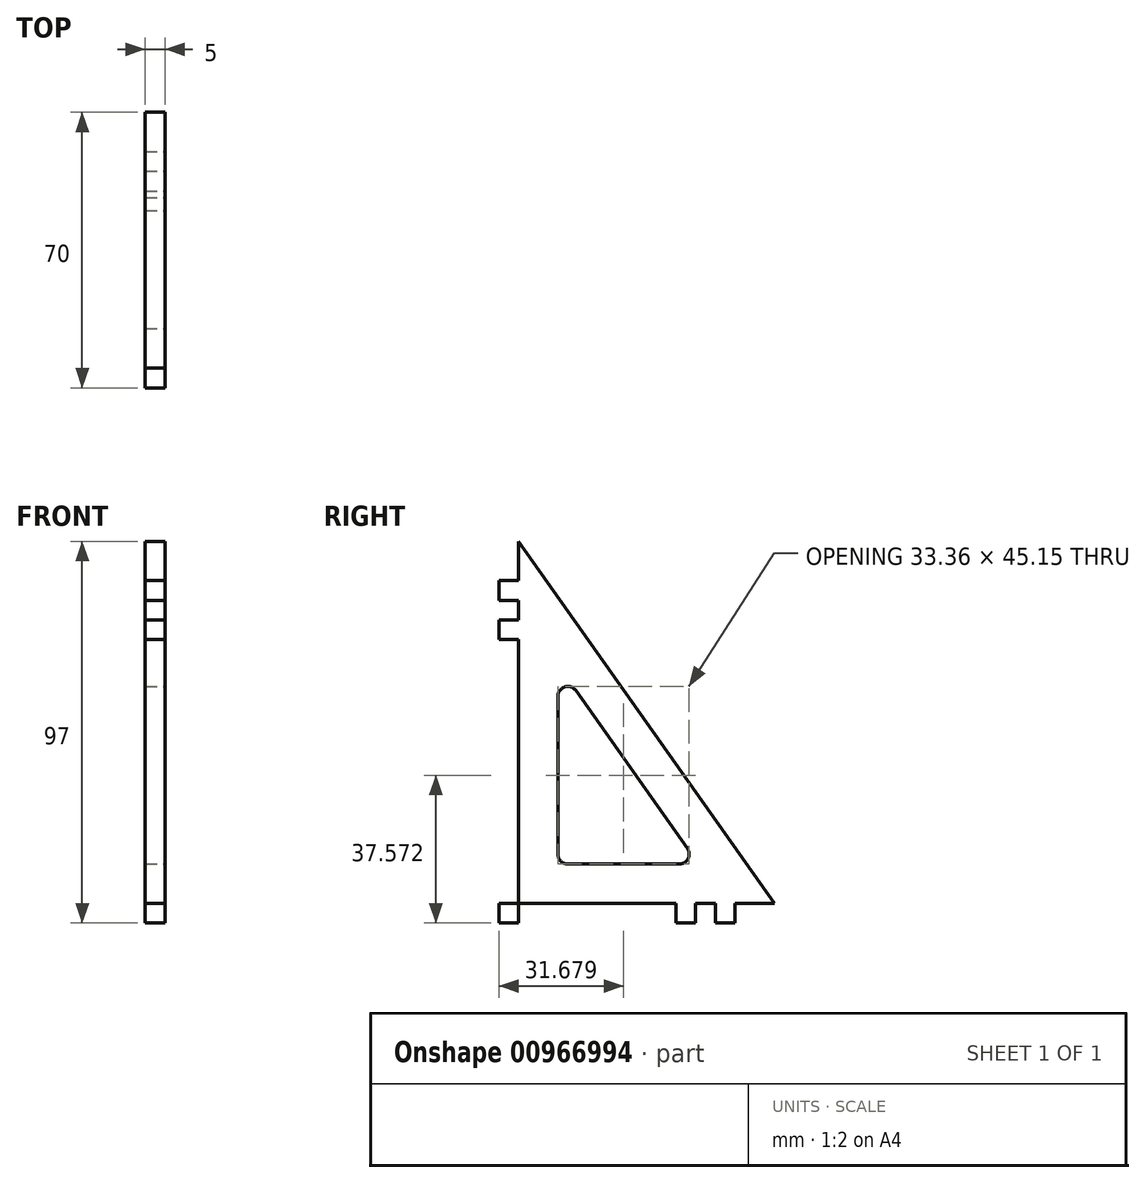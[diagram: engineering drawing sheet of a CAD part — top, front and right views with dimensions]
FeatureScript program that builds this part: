
annotation { "Feature Type Name" : "Feature", "Feature Type Description" : "" }
export const myFeature = defineFeature(function(context is Context, id is Id, definition is map)
    precondition{}
    {
        {
            var Q0;
            Q0=qCreatedBy(makeId("Right.planeOp"),FACE);
            var sketch = newSketch(context, id + "F0", { "sketchPlane" : qUnion([Q0])});
            skLineSegment(sketch, "E0", {"start": v(0, 97) * mm, "end": v(0, 0) * mm});
            skLineSegment(sketch, "E1", {"start": v(0, 0) * mm, "end": v(70, 0) * mm});
            skLineSegment(sketch, "E2", {"start": v(70, 0) * mm, "end": v(70, 5) * mm});
            skLineSegment(sketch, "E3", {"start": v(70, 5) * mm, "end": v(5, 97) * mm});
            skLineSegment(sketch, "E4", {"start": v(5, 97) * mm, "end": v(0, 97) * mm});
            skSolve(sketch);
        }
        {
            var Q0;
            Q0=makeQuery(id+"F0.imprint","IMPRINT",FACE,{"disambiguationData":[TD([[makeQuery(id+"F0.imprint","IMPRINT",EDGE,{"derivedFrom":sQuery(id+"F0.wireOp",EDGE,"E0")}),1.0]])]});
            extrude(context, id + "F1", {"entities" : qUnion([Q0]), "oppositeDirection" : true, "depth" : 5 * mm, "offsetDistance" : 25 * mm});
        }
        {
            var Q0;
            Q0=makeQuery(id+"F1.opExtrude","CAP_FACE",FACE,{"disambiguationData":[OSD([sQuery(id+"F0.wireOp",EDGE,"E0"),sQuery(id+"F0.wireOp",EDGE,"E1"),sQuery(id+"F0.wireOp",EDGE,"E2"),sQuery(id+"F0.wireOp",EDGE,"E3"),sQuery(id+"F0.wireOp",EDGE,"E4")])],"isStart":true});
            var sketch = newSketch(context, id + "F2", { "sketchPlane" : qUnion([Q0])});
            skLineSegment(sketch, "E5", {"start": v(15, 57.65) * mm, "end": v(15, 17.5) * mm});
            skLineSegment(sketch, "E6", {"start": v(17.5, 15) * mm, "end": v(45.86, 15) * mm});
            skLineSegment(sketch, "E7", {"start": v(47.9, 18.94) * mm, "end": v(19.54, 59.09) * mm});
            skPoint(sketch, "E8.visualSharp", {"position": v(15, 65.52) * mm});
            skArc(sketch, "E8.filletArc", {"start": v(19.54, 59.09) * mm, "mid": v(16.74, 60.03) * mm, "end": v(15, 57.65) * mm});
            skPoint(sketch, "E9.visualSharp", {"position": v(15, 15) * mm});
            skArc(sketch, "E9.filletArc", {"start": v(15, 17.5) * mm, "mid": v(15.73, 15.73) * mm, "end": v(17.5, 15) * mm});
            skPoint(sketch, "E10.visualSharp", {"position": v(50.7, 15) * mm});
            skArc(sketch, "E10.filletArc", {"start": v(45.86, 15) * mm, "mid": v(48.08, 16.35) * mm, "end": v(47.9, 18.94) * mm});
            skSolve(sketch);
        }
        {
            var Q0;
            Q0=makeQuery(id+"F2.imprint","IMPRINT",FACE,{"disambiguationData":[TD([[makeQuery(id+"F2.imprint","IMPRINT",EDGE,{"derivedFrom":sQuery(id+"F2.wireOp",EDGE,"E5")}),1.0]])]});
            extrude(context, id + "F3", {"entities" : qUnion([Q0]), "operationType" : NewBodyOperationType.REMOVE, "endBound" : BoundingType.THROUGH_ALL, "oppositeDirection" : true, "depth" : 25 * mm, "offsetDistance" : 25 * mm});
        }
        {
            var Q0;
            Q0=makeQuery(id+"F1.opExtrude","CAP_FACE",FACE,{"disambiguationData":[OSD([sQuery(id+"F0.wireOp",EDGE,"E0"),sQuery(id+"F0.wireOp",EDGE,"E1"),sQuery(id+"F0.wireOp",EDGE,"E2"),sQuery(id+"F0.wireOp",EDGE,"E3"),sQuery(id+"F0.wireOp",EDGE,"E4")])],"isStart":true});
            var sketch = newSketch(context, id + "F4", { "sketchPlane" : qUnion([Q0])});
            skLineSegment(sketch, "E11.bottom", {"start": v(0, 97) * mm, "end": v(5, 97) * mm});
            skLineSegment(sketch, "E11.top", {"start": v(0, 87) * mm, "end": v(5, 87) * mm});
            skLineSegment(sketch, "E11.left", {"start": v(0, 97) * mm, "end": v(0, 87) * mm});
            skLineSegment(sketch, "E11.right", {"start": v(5, 97) * mm, "end": v(5, 87) * mm});
            skLineSegment(sketch, "E12.bottom", {"start": v(0, 82) * mm, "end": v(5, 82) * mm});
            skLineSegment(sketch, "E12.top", {"start": v(0, 77) * mm, "end": v(5, 77) * mm});
            skLineSegment(sketch, "E12.left", {"start": v(0, 82) * mm, "end": v(0, 77) * mm});
            skLineSegment(sketch, "E12.right", {"start": v(5, 82) * mm, "end": v(5, 77) * mm});
            skLineSegment(sketch, "E13.bottom", {"start": v(0, 72) * mm, "end": v(5, 72) * mm});
            skLineSegment(sketch, "E13.top", {"start": v(0, 0) * mm, "end": v(5, 0) * mm});
            skLineSegment(sketch, "E13.left", {"start": v(0, 72) * mm, "end": v(0, 0) * mm});
            skLineSegment(sketch, "E13.right", {"start": v(5, 72) * mm, "end": v(5, 0) * mm});
            skLineSegment(sketch, "E14.bottom", {"start": v(70, 0) * mm, "end": v(60, 0) * mm});
            skLineSegment(sketch, "E14.top", {"start": v(70, 5) * mm, "end": v(60, 5) * mm});
            skLineSegment(sketch, "E14.left", {"start": v(70, 0) * mm, "end": v(70, 5) * mm});
            skLineSegment(sketch, "E14.right", {"start": v(60, 0) * mm, "end": v(60, 5) * mm});
            skLineSegment(sketch, "E15.bottom", {"start": v(55, 0) * mm, "end": v(50, 0) * mm});
            skLineSegment(sketch, "E15.top", {"start": v(55, 5) * mm, "end": v(50, 5) * mm});
            skLineSegment(sketch, "E15.left", {"start": v(55, 0) * mm, "end": v(55, 5) * mm});
            skLineSegment(sketch, "E15.right", {"start": v(50, 0) * mm, "end": v(50, 5) * mm});
            skLineSegment(sketch, "E16.bottom", {"start": v(45, 0) * mm, "end": v(0, 0) * mm});
            skLineSegment(sketch, "E16.top", {"start": v(45, 5) * mm, "end": v(0, 5) * mm});
            skLineSegment(sketch, "E16.left", {"start": v(45, 0) * mm, "end": v(45, 5) * mm});
            skLineSegment(sketch, "E16.right", {"start": v(0, 0) * mm, "end": v(0, 5) * mm});
            skSolve(sketch);
        }
        {
            var Q0;
            Q0=makeQuery(id+"F4.imprint","IMPRINT",FACE,{"disambiguationData":[TD([[makeQuery(id+"F4.imprint","IMPRINT",EDGE,{"derivedFrom":sQuery(id+"F4.wireOp",EDGE,"E11.bottom")}),1.0]])]});
            var Q1;
            Q1=makeQuery(id+"F4.imprint","IMPRINT",FACE,{"disambiguationData":[TD([[makeQuery(id+"F4.imprint","IMPRINT",EDGE,{"derivedFrom":sQuery(id+"F4.wireOp",EDGE,"E12.bottom")}),-1.0]])]});
            var Q2;
            {var subQ0=sQuery(id+"F4.wireOp",EDGE,"E13.bottom");Q2=makeQuery(id+"F4.imprint","IMPRINT",FACE,{"disambiguationData":[TD([[makeQuery(id+"F4.imprint","IMPRINT",EDGE,{"derivedFrom":subQ0}),-1.0]])]});}
            var Q3;
            {var subQ5=sQuery(id+"F4.wireOp",EDGE,"E16.left");Q3=makeQuery(id+"F4.imprint","IMPRINT",FACE,{"disambiguationData":[TD([[makeQuery(id+"F4.imprint","IMPRINT",EDGE,{"derivedFrom":subQ5}),1.0]])]});}
            var Q4;
            {var subQ5=sQuery(id+"F4.wireOp",EDGE,"E16.right");Q4=makeQuery(id+"F4.imprint","IMPRINT",FACE,{"disambiguationData":[TD([[makeQuery(id+"F4.imprint","IMPRINT",EDGE,{"derivedFrom":subQ5}),1.0]])]});}
            var Q5;
            Q5=makeQuery(id+"F4.imprint","IMPRINT",FACE,{"disambiguationData":[TD([[makeQuery(id+"F4.imprint","IMPRINT",EDGE,{"derivedFrom":sQuery(id+"F4.wireOp",EDGE,"E15.bottom")}),1.0]])]});
            var Q6;
            Q6=makeQuery(id+"F4.imprint","IMPRINT",FACE,{"disambiguationData":[TD([[makeQuery(id+"F4.imprint","IMPRINT",EDGE,{"derivedFrom":sQuery(id+"F4.wireOp",EDGE,"E14.bottom")}),1.0]])]});
            extrude(context, id + "F5", {"entities" : qUnion([Q0, Q1, Q2, Q3, Q4, Q5, Q6]), "operationType" : NewBodyOperationType.REMOVE, "endBound" : BoundingType.THROUGH_ALL, "oppositeDirection" : true, "depth" : 25 * mm, "offsetDistance" : 25 * mm});
        }
    });
